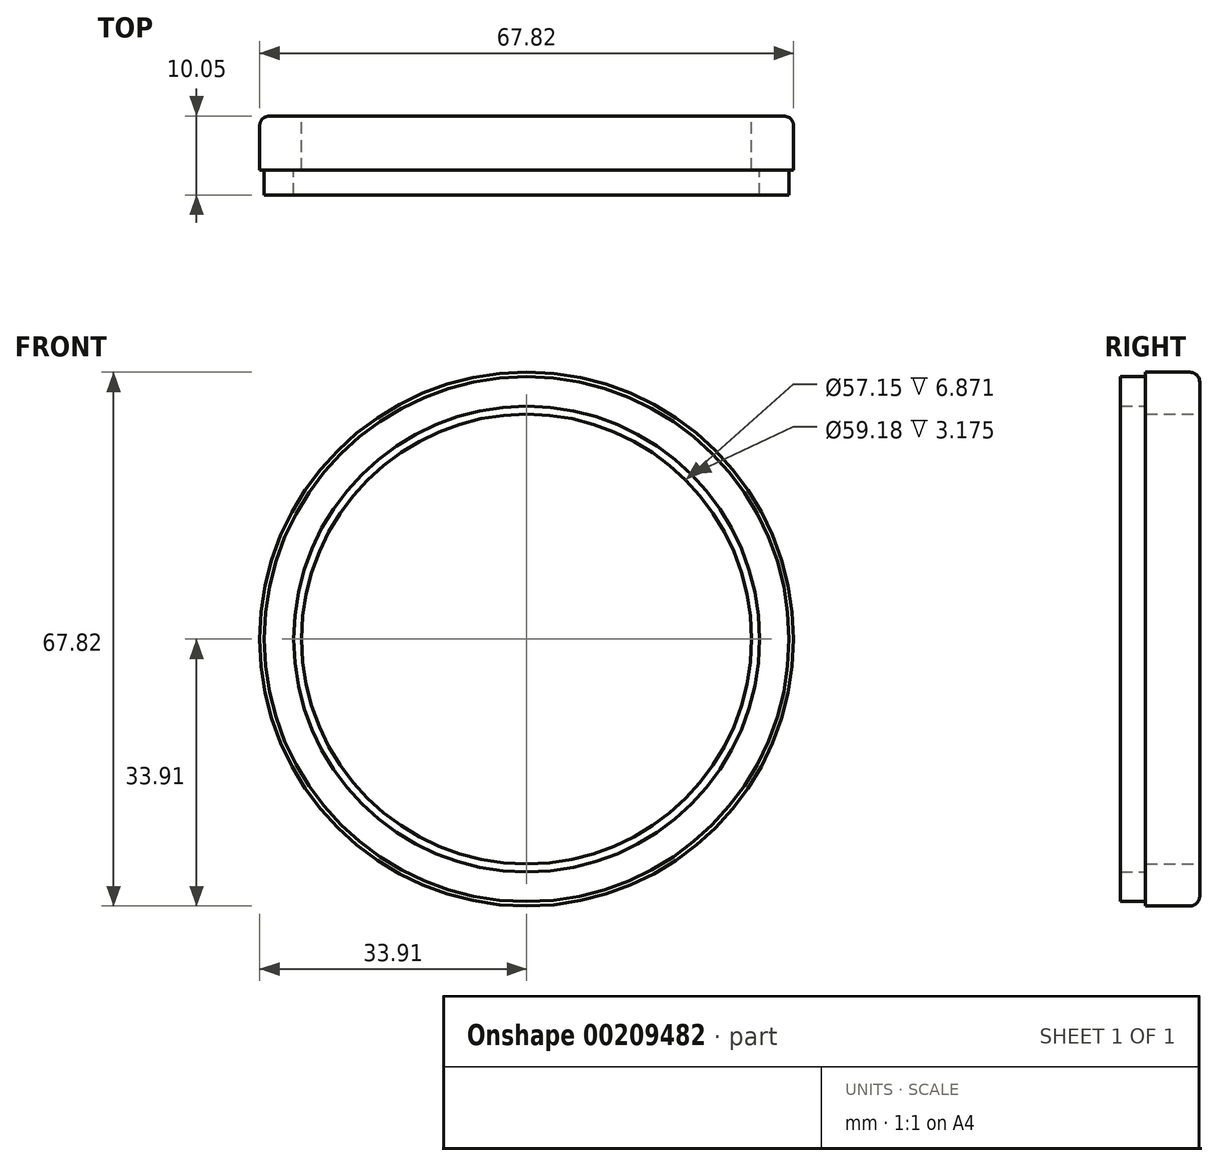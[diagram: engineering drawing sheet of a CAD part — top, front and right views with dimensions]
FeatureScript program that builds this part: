
annotation { "Feature Type Name" : "Feature", "Feature Type Description" : "" }
export const myFeature = defineFeature(function(context is Context, id is Id, definition is map)
    precondition{}
    {
        {
            var Q0;
            Q0=qCreatedBy(makeId("Front.planeOp"),FACE);
            var sketch = newSketch(context, id + "F0", { "sketchPlane" : qUnion([Q0])});
            skCircle(sketch, "E0", {"center": v(0, 0) * mm, "radius": 33.9 * mm});
            skCircle(sketch, "E1", {"center": v(0, 0) * mm, "radius": 28.58 * mm});
            skSolve(sketch);
        }
        {
            var Q0;
            Q0 = qSketchRegion(id + "F0", true);
            extrude(context, id + "F1", {"entities" : qUnion([Q0]), "depth" : 9.65 * mm});
        }
        {
            var Q0;
            Q0=makeQuery(id+"F1.opExtrude","CAP_FACE",FACE,{"disambiguationData":[OSD([sQuery(id+"F0.wireOp",EDGE,"E0"),sQuery(id+"F0.wireOp",EDGE,"E1")])],"isStart":false});
            var sketch = newSketch(context, id + "F2", { "sketchPlane" : qUnion([Q0])});
            skCircle(sketch, "E2", {"center": v(0, 0) * mm, "radius": 33.34 * mm});
            skCircle(sketch, "E3", {"center": v(0, 0) * mm, "radius": 26.74 * mm});
            skCircle(sketch, "E4", {"center": v(0, 0) * mm, "radius": 29.6 * mm});
            skSolve(sketch);
        }
        {
            var Q0;
            Q0 = qSketchRegion(id + "F2", true);
            extrude(context, id + "F3", {"entities" : qUnion([Q0]), "operationType" : NewBodyOperationType.ADD, "depth" : 4.7 * mm});
        }
        {
            var Q0;
            Q0=makeQuery(id+"F1.opExtrude","CAP_EDGE",EDGE,{"disambiguationData":[OSD([sQuery(id+"F0.wireOp",EDGE,"E0")])],"isStart":true});
            fillet(context, id + "F4", {"entities" : qUnion([Q0]), "radius" : 1.27 * mm, "tangentPropagation" : true, "allowEdgeOverflow" : false});
        }
        {
            var Q0;
            Q0=makeQuery(id+"F3.opExtrude","CAP_FACE",FACE,{"disambiguationData":[OSD([sQuery(id+"F2.wireOp",EDGE,"E2"),sQuery(id+"F2.wireOp",EDGE,"E4")])],"isStart":false});
            extrude(context, id + "F5", {"entities" : qUnion([Q0]), "operationType" : NewBodyOperationType.REMOVE, "oppositeDirection" : true, "depth" : 1.54 * mm});
        }
        {
            var Q0;
            Q0=makeQuery(id+"F5.boolean.opBoolean","COPY",FACE,{"derivedFrom":makeQuery(id+"F5.opExtrude","CAP_FACE",FACE,{"disambiguationData":[OSD([sQuery(id+"F2.wireOp",EDGE,"E2"),sQuery(id+"F2.wireOp",EDGE,"E4")])],"isStart":false})});
            extrude(context, id + "F6", {"entities" : qUnion([Q0]), "operationType" : NewBodyOperationType.REMOVE, "oppositeDirection" : true, "depth" : 2.77 * mm});
        }
        {
            var Q0;
            {var subQ0=sQuery(id+"F0.wireOp",EDGE,"E0");Q0=makeQuery(id+"F3.boolean.opBoolean","SPLIT",FACE,{"disambiguationData":[TD([makeQuery(id+"F1.opExtrude","SWEPT_FACE",FACE,{"disambiguationData":[OSD([subQ0])]})])],"derivedFrom":makeQuery(id+"F1.opExtrude","CAP_FACE",FACE,{"disambiguationData":[OSD([subQ0,sQuery(id+"F0.wireOp",EDGE,"E1")])],"isStart":false})});}
            var Q1;
            {var subQ0=sQuery(id+"F0.wireOp",EDGE,"E1");Q1=makeQuery(id+"F3.boolean.opBoolean","SPLIT",FACE,{"disambiguationData":[TD([makeQuery(id+"F1.opExtrude","SWEPT_FACE",FACE,{"disambiguationData":[OSD([subQ0])]})])],"derivedFrom":makeQuery(id+"F1.opExtrude","CAP_FACE",FACE,{"disambiguationData":[OSD([sQuery(id+"F0.wireOp",EDGE,"E0"),subQ0])],"isStart":false})});}
            extrude(context, id + "F7", {"entities" : qUnion([Q0, Q1]), "operationType" : NewBodyOperationType.REMOVE, "oppositeDirection" : true, "depth" : 2.78 * mm});
        }
    });
